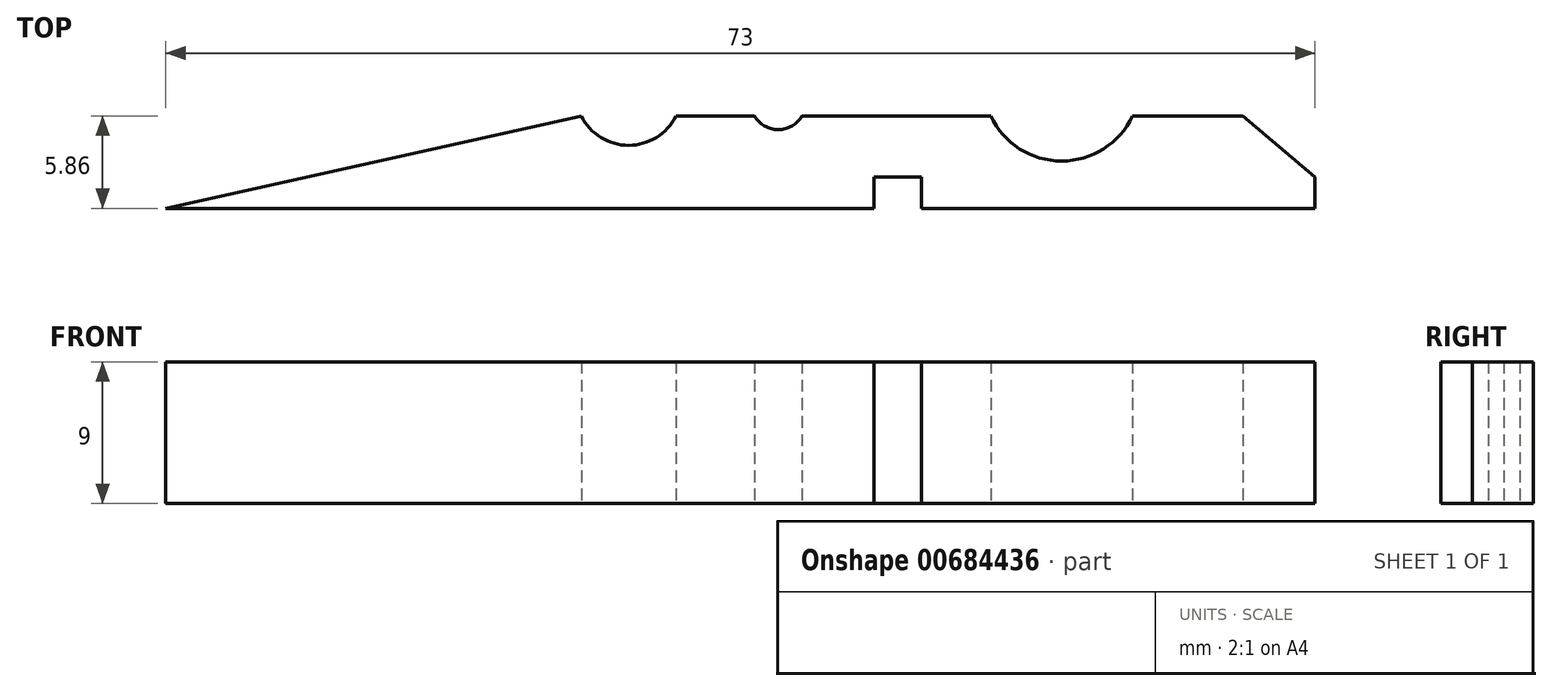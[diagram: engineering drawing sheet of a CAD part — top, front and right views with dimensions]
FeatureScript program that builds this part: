
annotation { "Feature Type Name" : "Feature", "Feature Type Description" : "" }
export const myFeature = defineFeature(function(context is Context, id is Id, definition is map)
    precondition{}
    {
        {
            var Q0;
            Q0=qCreatedBy(makeId("Top.planeOp"),FACE);
            var sketch = newSketch(context, id + "F0", { "sketchPlane" : qUnion([Q0])});
            skLineSegment(sketch, "E0", {"start": v(0, 0) * mm, "end": v(-45, 0) * mm});
            skLineSegment(sketch, "E1", {"start": v(0, 0) * mm, "end": v(0, 2) * mm});
            skLineSegment(sketch, "E2", {"start": v(0, 2) * mm, "end": v(3, 2) * mm});
            skLineSegment(sketch, "E3", {"start": v(3, 2) * mm, "end": v(3, 0) * mm});
            skLineSegment(sketch, "E4", {"start": v(3, 0) * mm, "end": v(28, 0) * mm});
            skLineSegment(sketch, "E5", {"start": v(28, 0) * mm, "end": v(28, 2) * mm});
            skLineSegment(sketch, "E6", {"start": v(28, 2) * mm, "end": v(23.4, 5.86) * mm});
            skLineSegment(sketch, "E7", {"start": v(23.4, 5.86) * mm, "end": v(16.4, 5.86) * mm});
            skArc(sketch, "E8", {"start": v(7.4, 5.86) * mm, "mid": v(11.9, 3) * mm, "end": v(16.4, 5.86) * mm});
            skLineSegment(sketch, "E9", {"start": v(7.4, 5.86) * mm, "end": v(-4.6, 5.86) * mm});
            skArc(sketch, "E10", {"start": v(-7.6, 5.86) * mm, "mid": v(-6.1, 5) * mm, "end": v(-4.6, 5.86) * mm});
            skLineSegment(sketch, "E11", {"start": v(-7.6, 5.86) * mm, "end": v(-12.6, 5.86) * mm});
            skArc(sketch, "E12", {"start": v(-18.6, 5.86) * mm, "mid": v(-15.6, 4) * mm, "end": v(-12.6, 5.86) * mm});
            skLineSegment(sketch, "E13", {"start": v(-18.6, 5.86) * mm, "end": v(-45, 0) * mm});
            skSolve(sketch);
        }
        {
            var Q0;
            Q0=makeQuery(id+"F0.imprint","IMPRINT",FACE,{"disambiguationData":[TD([[makeQuery(id+"F0.imprint","IMPRINT",EDGE,{"derivedFrom":sQuery(id+"F0.wireOp",EDGE,"E0")}),-1.0]])]});
            extrude(context, id + "F1", {"entities" : qUnion([Q0]), "depth" : 9 * mm, "offsetDistance" : 25 * mm});
        }
    });
